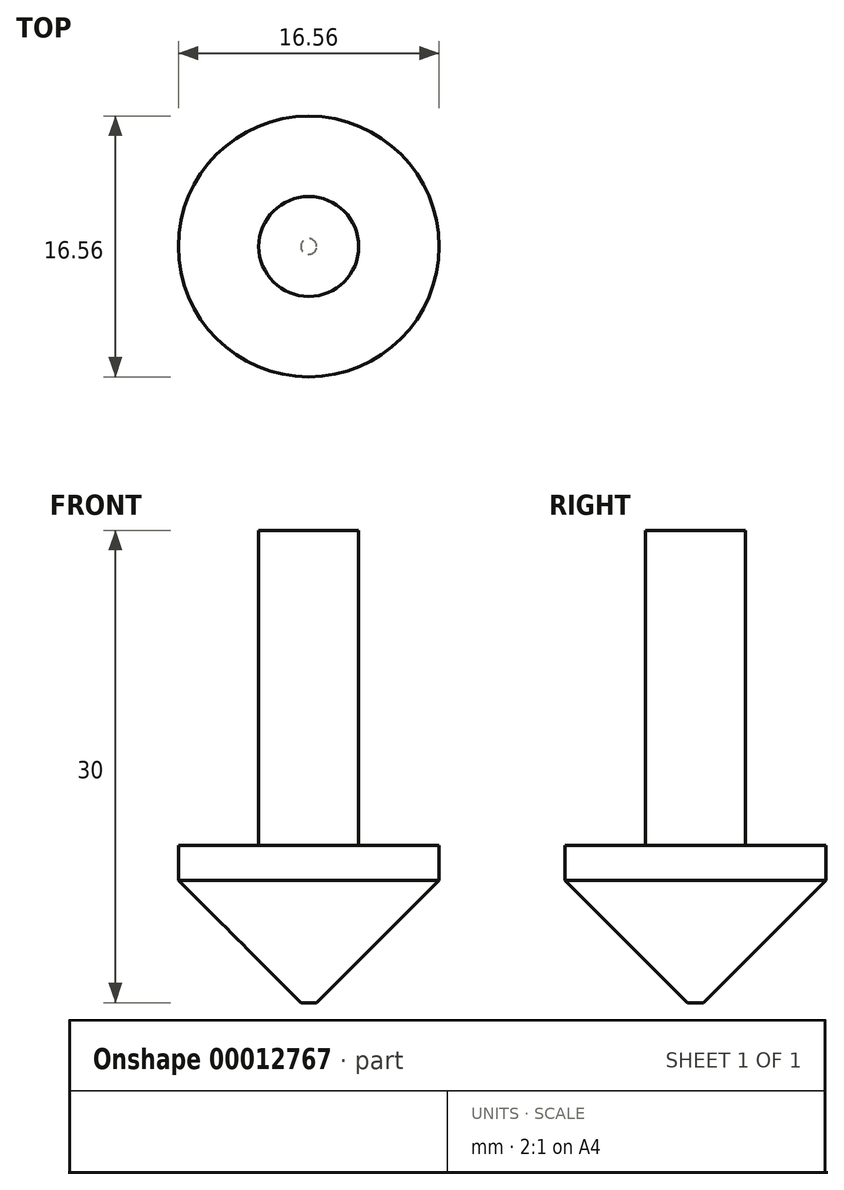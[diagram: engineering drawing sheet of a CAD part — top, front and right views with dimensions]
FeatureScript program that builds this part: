
annotation { "Feature Type Name" : "Feature", "Feature Type Description" : "" }
export const myFeature = defineFeature(function(context is Context, id is Id, definition is map)
    precondition{}
    {
        {
            var Q0;
            Q0=qCreatedBy(makeId("Front.planeOp"),FACE);
            var sketch = newSketch(context, id + "F0", { "sketchPlane" : qUnion([Q0])});
            skLineSegment(sketch, "E0.bottom", {"start": v(0, 0) * mm, "end": v(-3.17, 0) * mm});
            skLineSegment(sketch, "E0.top", {"start": v(0, 20) * mm, "end": v(-3.18, 20) * mm});
            skLineSegment(sketch, "E0.left", {"start": v(0, 0) * mm, "end": v(0, 20) * mm});
            skLineSegment(sketch, "E0.right", {"start": v(-3.17, 0) * mm, "end": v(-3.18, 20) * mm});
            skLineSegment(sketch, "E1", {"start": v(-3.17, 0) * mm, "end": v(-8.28, 0) * mm});
            skLineSegment(sketch, "E2", {"start": v(-8.28, 0) * mm, "end": v(-8.28, -2.22) * mm});
            skLineSegment(sketch, "E3", {"start": v(-8.28, -2.22) * mm, "end": v(-0.5, -10) * mm});
            skLineSegment(sketch, "E4", {"start": v(-0.5, -10) * mm, "end": v(0, -10) * mm});
            skLineSegment(sketch, "E5", {"start": v(0, -10) * mm, "end": v(0, 0) * mm});
            skSolve(sketch);
        }
        {
            var Q0;
            Q0=makeQuery(id+"F0.imprint","IMPRINT",FACE,{"disambiguationData":[TD([[makeQuery(id+"F0.imprint","IMPRINT",EDGE,{"derivedFrom":sQuery(id+"F0.wireOp",EDGE,"E0.bottom")}),1.0]])]});
            var Q1;
            Q1=makeQuery(id+"F0.imprint","IMPRINT",FACE,{"disambiguationData":[TD([[makeQuery(id+"F0.imprint","IMPRINT",EDGE,{"derivedFrom":sQuery(id+"F0.wireOp",EDGE,"E0.bottom")}),-1.0]])]});
            var Q2;
            Q2=sQuery(id+"F0.wireOp",EDGE,"E0.top");
            var Q3;
            Q3=sQuery(id+"F0.wireOp",EDGE,"E0.right");
            var Q4;
            Q4=sQuery(id+"F0.wireOp",EDGE,"E1");
            var Q5;
            Q5=sQuery(id+"F0.wireOp",EDGE,"E2");
            var Q6;
            Q6=sQuery(id+"F0.wireOp",EDGE,"E3");
            var Q7;
            Q7=sQuery(id+"F0.wireOp",EDGE,"E4");
            var Q8;
            Q8=sQuery(id+"F0.wireOp",EDGE,"E0.left");
            revolve(context, id + "F1", {"entities" : qUnion([Q0, Q1]), "surfaceEntities" : qUnion([Q2, Q3, Q4, Q5, Q6, Q7]), "axis" : qUnion([Q8]), "revolveType" : RevolveType.FULL});
        }
    });
